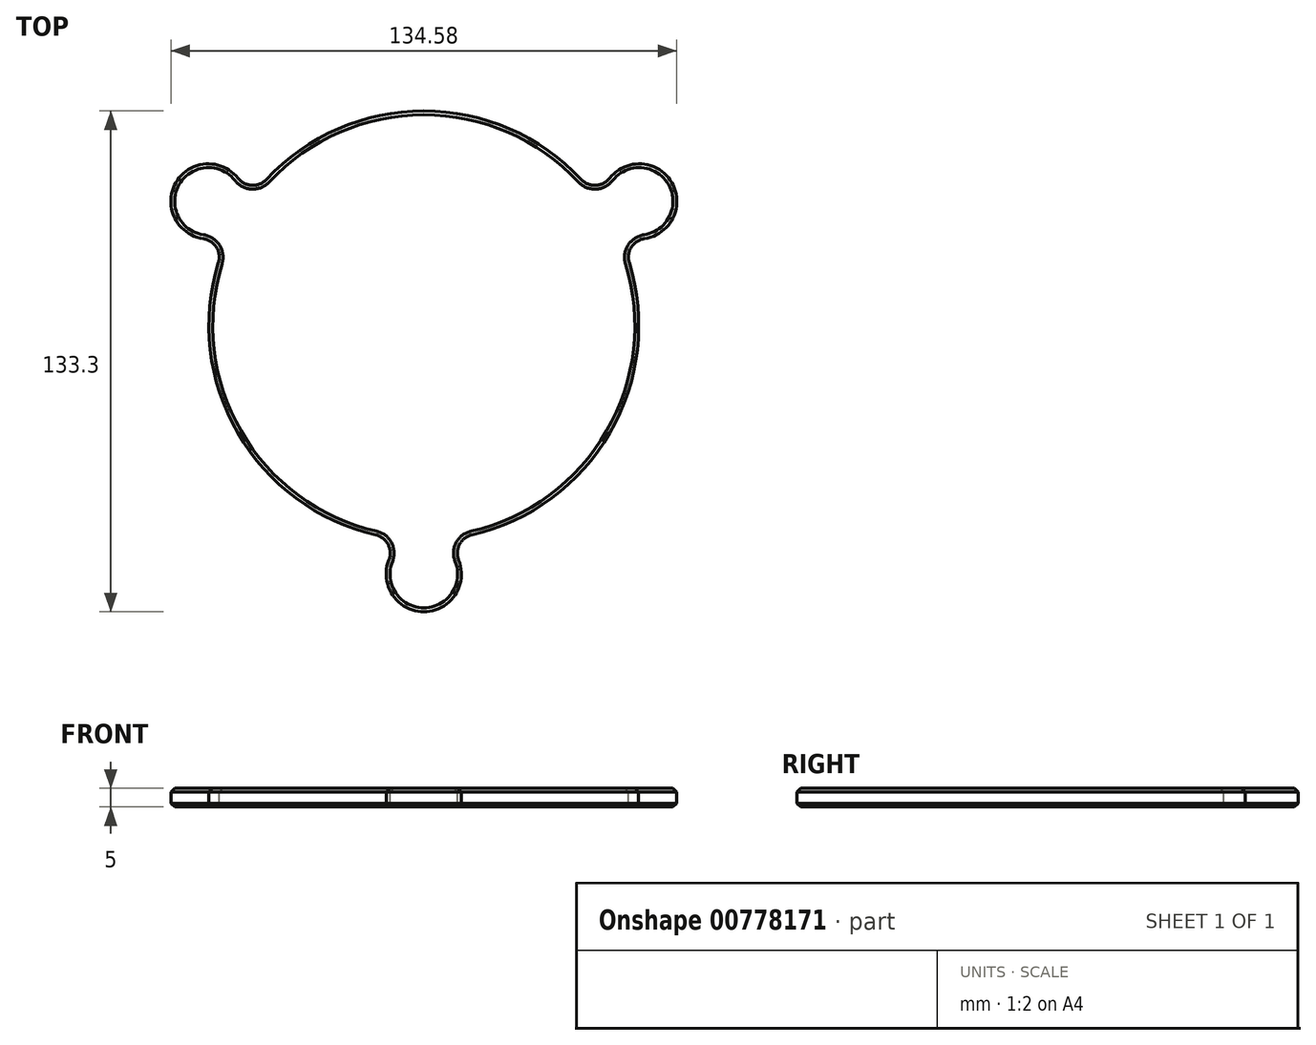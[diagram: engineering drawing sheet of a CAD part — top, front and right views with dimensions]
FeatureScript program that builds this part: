
annotation { "Feature Type Name" : "Feature", "Feature Type Description" : "" }
export const myFeature = defineFeature(function(context is Context, id is Id, definition is map)
    precondition{}
    {
        {
            var Q0;
            Q0=qCreatedBy(makeId("Top.planeOp"),FACE);
            var sketch = newSketch(context, id + "F0", { "sketchPlane" : qUnion([Q0])});
            skCircle(sketch, "E0", {"center": v(0, 0) * mm, "radius": 57.15 * mm});
            skArc(sketch, "E1", {"start": v(-4.05, -57) * mm, "mid": v(0, -76.15) * mm, "end": v(4.05, -57) * mm});
            skArc(sketch, "E2.1.0", {"start": v(51.4, 25) * mm, "mid": v(65.95, 38.07) * mm, "end": v(47.34, 32) * mm});
            skArc(sketch, "E2.2.0", {"start": v(-47.34, 32) * mm, "mid": v(-65.95, 38.08) * mm, "end": v(-51.4, 25) * mm});
            skSolve(sketch);
        }
        {
            var Q0;
            {var subQ0=sQuery(id+"F0.wireOp",EDGE,"E1");Q0=makeQuery(id+"F0.imprint","IMPRINT",FACE,{"disambiguationData":[TD([[makeQuery(id+"F0.imprint","IMPRINT",EDGE,{"derivedFrom":subQ0}),1.0]])]});}
            var Q1;
            {var subQ1=sQuery(id+"F0.wireOp",EDGE,"E0");var subQ6=sQuery(id+"F0.wireOp",EDGE,"E2.1.0");var subQ8=makeQuery(id+"F0.imprint","INTERSECT",VERTEX,{"disambiguationData":[OD(0.0)],"derivedFrom":[subQ1,subQ6]});Q1=makeQuery(id+"F0.imprint","IMPRINT",FACE,{"disambiguationData":[TD([[makeQuery(id+"F0.imprint","IMPRINT",EDGE,{"disambiguationData":[TD([[subQ8,-1.0]])],"derivedFrom":subQ1}),1.0]])]});}
            var Q2;
            {var subQ0=sQuery(id+"F0.wireOp",EDGE,"E2.1.0");Q2=makeQuery(id+"F0.imprint","IMPRINT",FACE,{"disambiguationData":[TD([[makeQuery(id+"F0.imprint","IMPRINT",EDGE,{"derivedFrom":subQ0}),1.0]])]});}
            var Q3;
            {var subQ0=sQuery(id+"F0.wireOp",EDGE,"E2.2.0");Q3=makeQuery(id+"F0.imprint","IMPRINT",FACE,{"disambiguationData":[TD([[makeQuery(id+"F0.imprint","IMPRINT",EDGE,{"derivedFrom":subQ0}),1.0]])]});}
            extrude(context, id + "F1", {"entities" : qUnion([Q0, Q1, Q2, Q3]), "depth" : 5 * mm, "offsetDistance" : 25 * mm});
        }
        {
            var Q0;
            {var subQ0=sQuery(id+"F0.wireOp",EDGE,"E1");var subQ1=sQuery(id+"F0.wireOp",EDGE,"E0");Q0=makeQuery(id+"F1.opExtrude","SWEPT_EDGE",EDGE,{"disambiguationData":[OSD([subQ1,subQ0]),TDD([makeQuery(id+"F0.imprint","INTERSECT",VERTEX,{"disambiguationData":[OD(0.0)],"derivedFrom":[subQ1,subQ0]})])]});}
            var Q1;
            {var subQ0=sQuery(id+"F0.wireOp",EDGE,"E1");var subQ1=sQuery(id+"F0.wireOp",EDGE,"E0");Q1=makeQuery(id+"F1.opExtrude","SWEPT_EDGE",EDGE,{"disambiguationData":[OSD([subQ1,subQ0]),TDD([makeQuery(id+"F0.imprint","INTERSECT",VERTEX,{"disambiguationData":[OD(1.0)],"derivedFrom":[subQ1,subQ0]})])]});}
            var Q2;
            {var subQ0=sQuery(id+"F0.wireOp",EDGE,"E2.1.0");var subQ1=sQuery(id+"F0.wireOp",EDGE,"E0");Q2=makeQuery(id+"F1.opExtrude","SWEPT_EDGE",EDGE,{"disambiguationData":[OSD([subQ1,subQ0]),TDD([makeQuery(id+"F0.imprint","INTERSECT",VERTEX,{"disambiguationData":[OD(0.0)],"derivedFrom":[subQ1,subQ0]})])]});}
            var Q3;
            {var subQ0=sQuery(id+"F0.wireOp",EDGE,"E2.1.0");var subQ1=sQuery(id+"F0.wireOp",EDGE,"E0");Q3=makeQuery(id+"F1.opExtrude","SWEPT_EDGE",EDGE,{"disambiguationData":[OSD([subQ1,subQ0]),TDD([makeQuery(id+"F0.imprint","INTERSECT",VERTEX,{"disambiguationData":[OD(1.0)],"derivedFrom":[subQ1,subQ0]})])]});}
            var Q4;
            {var subQ0=sQuery(id+"F0.wireOp",EDGE,"E2.2.0");var subQ1=sQuery(id+"F0.wireOp",EDGE,"E0");Q4=makeQuery(id+"F1.opExtrude","SWEPT_EDGE",EDGE,{"disambiguationData":[OSD([subQ1,subQ0]),TDD([makeQuery(id+"F0.imprint","INTERSECT",VERTEX,{"disambiguationData":[OD(0.0)],"derivedFrom":[subQ1,subQ0]})])]});}
            var Q5;
            {var subQ0=sQuery(id+"F0.wireOp",EDGE,"E2.2.0");var subQ1=sQuery(id+"F0.wireOp",EDGE,"E0");Q5=makeQuery(id+"F1.opExtrude","SWEPT_EDGE",EDGE,{"disambiguationData":[OSD([subQ1,subQ0]),TDD([makeQuery(id+"F0.imprint","INTERSECT",VERTEX,{"disambiguationData":[OD(1.0)],"derivedFrom":[subQ1,subQ0]})])]});}
            fillet(context, id + "F2", {"entities" : qUnion([Q0, Q1, Q2, Q3, Q4, Q5]), "radius" : 5 * mm, "tangentPropagation" : true, "allowEdgeOverflow" : false});
        }
        {
            var Q0;
            Q0=makeQuery(id+"F1.opExtrude","CAP_FACE",FACE,{"disambiguationData":[OSD([sQuery(id+"F0.wireOp",EDGE,"E0"),sQuery(id+"F0.wireOp",EDGE,"E1"),sQuery(id+"F0.wireOp",EDGE,"E2.1.0"),sQuery(id+"F0.wireOp",EDGE,"E2.2.0")])],"isStart":false});
            var Q1;
            Q1=makeQuery(id+"F1.opExtrude","CAP_FACE",FACE,{"disambiguationData":[OSD([sQuery(id+"F0.wireOp",EDGE,"E0"),sQuery(id+"F0.wireOp",EDGE,"E1"),sQuery(id+"F0.wireOp",EDGE,"E2.1.0"),sQuery(id+"F0.wireOp",EDGE,"E2.2.0")])],"isStart":true});
            chamfer(context, id + "F3", {"entities" : qUnion([Q0, Q1]), "width" : 1 * mm, "tangentPropagation" : true});
        }
    });
